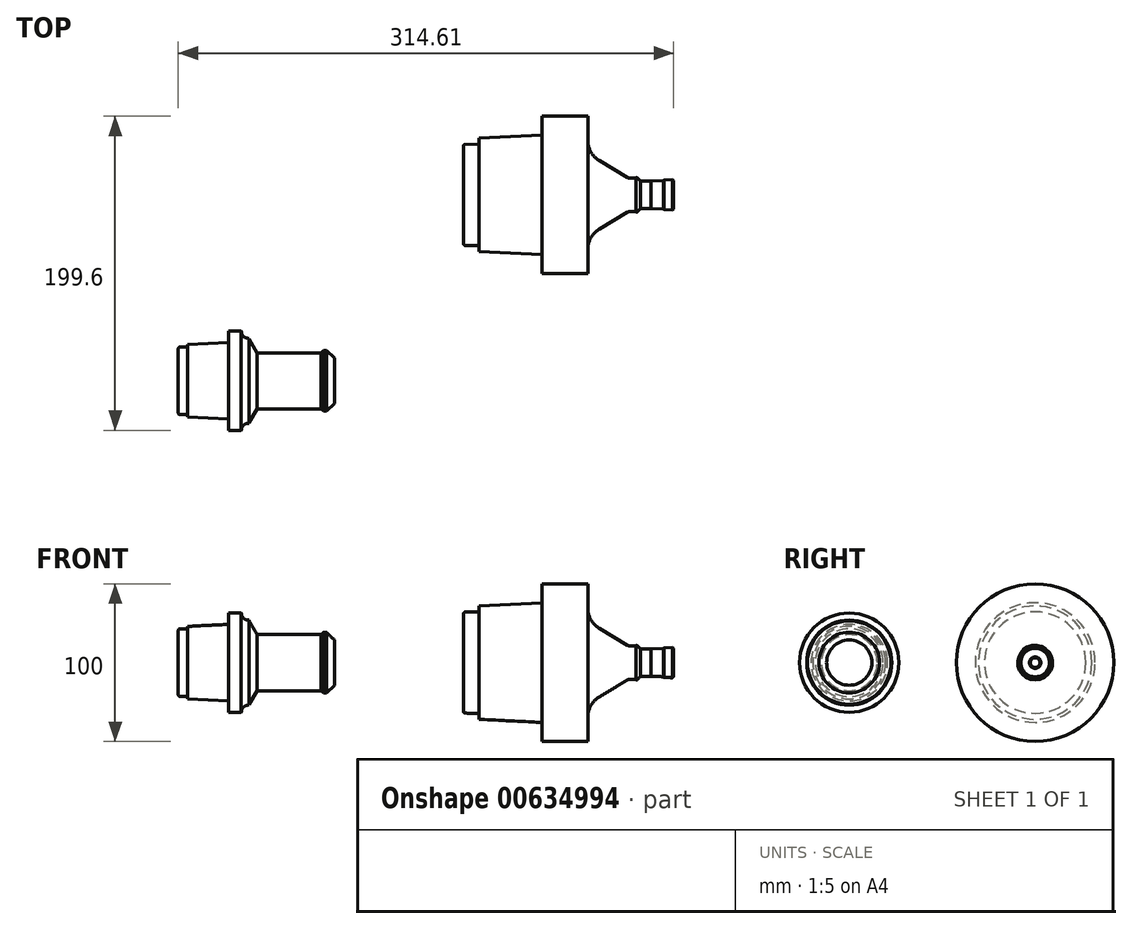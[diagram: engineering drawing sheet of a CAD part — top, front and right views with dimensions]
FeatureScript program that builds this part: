
annotation { "Feature Type Name" : "Feature", "Feature Type Description" : "" }
export const myFeature = defineFeature(function(context is Context, id is Id, definition is map)
    precondition{}
    {
        {
            var Q0;
            Q0=qCreatedBy(makeId("Top.planeOp"),FACE);
            var sketch = newSketch(context, id + "F0", { "sketchPlane" : qUnion([Q0])});
            skLineSegment(sketch, "E0", {"start": v(210.53, 152.35) * mm, "end": v(210.53, 136.99) * mm});
            skLineSegment(sketch, "E1", {"start": v(217.8, 124.13) * mm, "end": v(235.8, 113.32) * mm});
            skLineSegment(sketch, "E2", {"start": v(236.82, 113.03) * mm, "end": v(241.03, 113.03) * mm});
            skLineSegment(sketch, "E3", {"start": v(241.03, 113.03) * mm, "end": v(241.28, 113.29) * mm});
            skLineSegment(sketch, "E4", {"start": v(241.85, 113.29) * mm, "end": v(244.1, 111.03) * mm});
            skLineSegment(sketch, "E5", {"start": v(244.1, 111.03) * mm, "end": v(250.62, 111.03) * mm});
            skLineSegment(sketch, "E6", {"start": v(250.62, 111.03) * mm, "end": v(258.44, 111.3) * mm});
            skLineSegment(sketch, "E7", {"start": v(258.44, 111.3) * mm, "end": v(258.85, 111.74) * mm});
            skLineSegment(sketch, "E8", {"start": v(258.85, 111.74) * mm, "end": v(264.34, 111.95) * mm});
            skLineSegment(sketch, "E9", {"start": v(264.34, 111.95) * mm, "end": v(264.87, 111.45) * mm});
            skLineSegment(sketch, "E10", {"start": v(264.87, 111.45) * mm, "end": v(265.07, 105.96) * mm});
            skLineSegment(sketch, "E11", {"start": v(265.07, 105.96) * mm, "end": v(264.58, 105.43) * mm});
            skLineSegment(sketch, "E12", {"start": v(264.58, 105.43) * mm, "end": v(264.13, 105.41) * mm});
            skLineSegment(sketch, "E13", {"start": v(264.13, 105.41) * mm, "end": v(264.13, 102.35) * mm});
            skArc(sketch, "E14", {"start": v(241.85, 113.29) * mm, "mid": v(241.57, 113.4) * mm, "end": v(241.28, 113.29) * mm});
            skArc(sketch, "E15", {"start": v(235.8, 113.32) * mm, "mid": v(236.29, 113.1) * mm, "end": v(236.82, 113.03) * mm});
            skArc(sketch, "E16", {"start": v(210.53, 136.99) * mm, "mid": v(212.47, 129.6) * mm, "end": v(217.8, 124.13) * mm});
            skLineSegment(sketch, "E17", {"start": v(264.13, 102.35) * mm, "end": v(131.63, 102.35) * mm});
            skLineSegment(sketch, "E18", {"start": v(131.63, 102.35) * mm, "end": v(131.63, 133.43) * mm});
            skLineSegment(sketch, "E19", {"start": v(141.53, 134.56) * mm, "end": v(132.61, 134.43) * mm});
            skArc(sketch, "E20", {"start": v(132.61, 134.43) * mm, "mid": v(131.92, 134.13) * mm, "end": v(131.63, 133.43) * mm});
            skLineSegment(sketch, "E21", {"start": v(141.53, 134.56) * mm, "end": v(141.52, 138.35) * mm});
            skLineSegment(sketch, "E22", {"start": v(141.52, 138.35) * mm, "end": v(181.53, 140.35) * mm});
            skLineSegment(sketch, "E23", {"start": v(181.53, 140.35) * mm, "end": v(181.53, 152.35) * mm});
            skLineSegment(sketch, "E24", {"start": v(181.53, 152.35) * mm, "end": v(210.53, 152.35) * mm});
            skSolve(sketch);
        }
        {
            var Q0;
            Q0=makeQuery(id+"F0.imprint","IMPRINT",FACE,{"disambiguationData":[TD([[makeQuery(id+"F0.imprint","IMPRINT",EDGE,{"derivedFrom":sQuery(id+"F0.wireOp",EDGE,"E0")}),-1.0]])]});
            var Q1;
            Q1=sQuery(id+"F0.wireOp",EDGE,"E17");
            revolve(context, id + "F1", {"entities" : qUnion([Q0]), "axis" : qUnion([Q1]), "revolveType" : RevolveType.FULL});
        }
        {
            var Q0;
            Q0=qCreatedBy(makeId("Top.planeOp"),FACE);
            var sketch = newSketch(context, id + "F2", { "sketchPlane" : qUnion([Q0])});
            skLineSegment(sketch, "E25", {"start": v(-49.54, -15.75) * mm, "end": v(-49.54, 4.77) * mm});
            skLineSegment(sketch, "E26", {"start": v(-43.54, 5.77) * mm, "end": v(-48.54, 5.77) * mm});
            skLineSegment(sketch, "E27", {"start": v(-43.54, 5.77) * mm, "end": v(-43.54, 7.27) * mm});
            skLineSegment(sketch, "E28", {"start": v(-43.54, 7.27) * mm, "end": v(-17.54, 8.56) * mm});
            skLineSegment(sketch, "E29", {"start": v(-17.54, 8.56) * mm, "end": v(-17.54, 15.75) * mm});
            skLineSegment(sketch, "E30", {"start": v(-17.54, 15.75) * mm, "end": v(-9.54, 15.75) * mm});
            skLineSegment(sketch, "E31", {"start": v(-4.54, 10.75) * mm, "end": v(-4.54, 11.25) * mm});
            skLineSegment(sketch, "E32", {"start": v(-4.54, 10.75) * mm, "end": v(0.47, 2.07) * mm});
            skLineSegment(sketch, "E33", {"start": v(0.47, 2.07) * mm, "end": v(41.15, 2.07) * mm});
            skLineSegment(sketch, "E34", {"start": v(41.15, 2.07) * mm, "end": v(42.62, 3.53) * mm});
            skLineSegment(sketch, "E35", {"start": v(42.62, 3.53) * mm, "end": v(44.62, 3.53) * mm});
            skLineSegment(sketch, "E36", {"start": v(44.62, 3.53) * mm, "end": v(49.54, -1.37) * mm});
            skLineSegment(sketch, "E37", {"start": v(49.54, -1.37) * mm, "end": v(49.54, -15.75) * mm});
            skLineSegment(sketch, "E38", {"start": v(-4.54, 11.25) * mm, "end": v(-5.04, 11.25) * mm});
            skArc(sketch, "E39", {"start": v(-9.54, 15.75) * mm, "mid": v(-8.22, 12.57) * mm, "end": v(-5.04, 11.25) * mm});
            skArc(sketch, "E40", {"start": v(-48.54, 5.77) * mm, "mid": v(-49.25, 5.47) * mm, "end": v(-49.54, 4.77) * mm});
            skLineSegment(sketch, "E41", {"start": v(-49.54, -15.75) * mm, "end": v(49.54, -15.75) * mm});
            skSolve(sketch);
        }
        {
            var Q0;
            Q0=makeQuery(id+"F2.imprint","IMPRINT",FACE,{"disambiguationData":[TD([[makeQuery(id+"F2.imprint","IMPRINT",EDGE,{"derivedFrom":sQuery(id+"F2.wireOp",EDGE,"E25")}),-1.0]])]});
            var Q1;
            Q1 = qSketchRegion(id + "F2", true);
            var Q2;
            Q2=sQuery(id+"F2.wireOp",EDGE,"E41");
            var Q3;
            Q3=sQuery(id+"F2.wireOp",EDGE,"E37");
            var Q4;
            Q4=sQuery(id+"F2.wireOp",EDGE,"E36");
            var Q5;
            Q5=sQuery(id+"F2.wireOp",EDGE,"E35");
            var Q6;
            Q6=sQuery(id+"F2.wireOp",EDGE,"E34");
            var Q7;
            Q7=sQuery(id+"F2.wireOp",EDGE,"E33");
            var Q8;
            Q8=sQuery(id+"F2.wireOp",EDGE,"E32");
            var Q9;
            Q9=sQuery(id+"F2.wireOp",EDGE,"E39");
            var Q10;
            Q10=sQuery(id+"F2.wireOp",EDGE,"E30");
            var Q11;
            Q11=sQuery(id+"F2.wireOp",EDGE,"E29");
            var Q12;
            Q12=sQuery(id+"F2.wireOp",EDGE,"E28");
            var Q13;
            Q13=sQuery(id+"F2.wireOp",EDGE,"E27");
            var Q14;
            Q14=sQuery(id+"F2.wireOp",EDGE,"E26");
            var Q15;
            Q15=sQuery(id+"F2.wireOp",EDGE,"E40");
            var Q16;
            Q16=sQuery(id+"F2.wireOp",EDGE,"E25");
            var Q17;
            Q17=sQuery(id+"F2.wireOp",EDGE,"E38");
            var Q18;
            Q18=sQuery(id+"F2.wireOp",EDGE,"E31");
            var Q19;
            Q19=sQuery(id+"F2.wireOp",EDGE,"E41");
            revolve(context, id + "F3", {"entities" : qUnion([Q0, Q1]), "surfaceEntities" : qUnion([Q2, Q3, Q4, Q5, Q6, Q7, Q8, Q9, Q10, Q11, Q12, Q13, Q14, Q15, Q16, Q17, Q18]), "axis" : qUnion([Q19]), "revolveType" : RevolveType.FULL});
        }
    });
